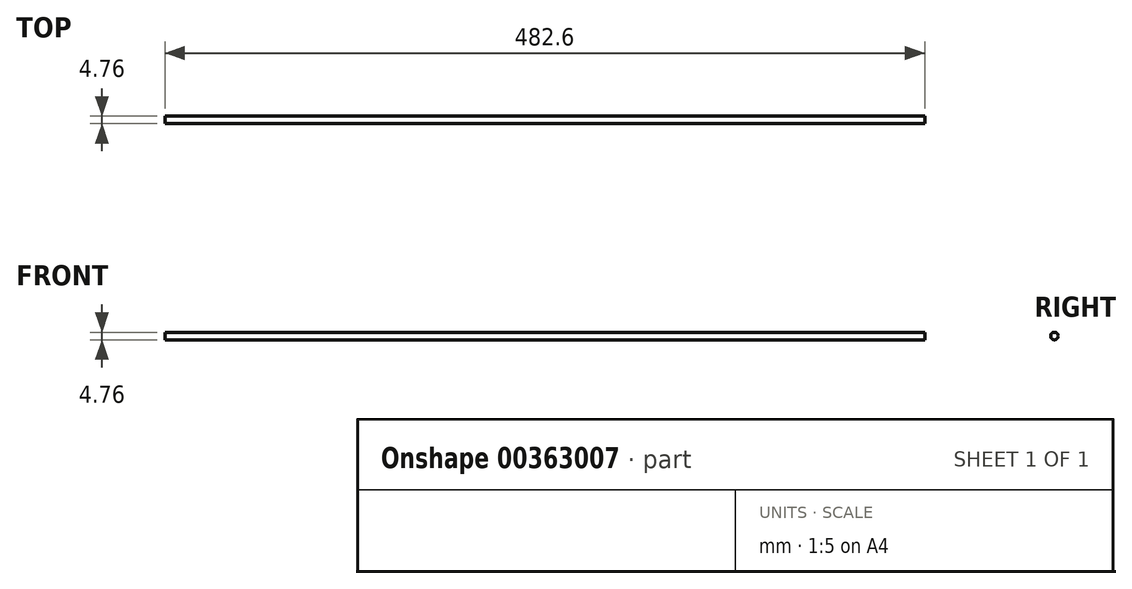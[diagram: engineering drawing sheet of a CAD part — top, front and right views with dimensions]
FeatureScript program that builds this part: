
annotation { "Feature Type Name" : "Feature", "Feature Type Description" : "" }
export const myFeature = defineFeature(function(context is Context, id is Id, definition is map)
    precondition{}
    {
        {
            var Q0;
            Q0=qCreatedBy(makeId("Right.planeOp"),FACE);
            var sketch = newSketch(context, id + "F0", { "sketchPlane" : qUnion([Q0])});
            skCircle(sketch, "E0", {"center": v(0, 0) * mm, "radius": 2.38 * mm});
            skSolve(sketch);
        }
        {
            var Q0;
            Q0=makeQuery(id+"F0.imprint","IMPRINT",FACE,{"disambiguationData":[TD([[makeQuery(id+"F0.imprint","IMPRINT",EDGE,{"derivedFrom":sQuery(id+"F0.wireOp",EDGE,"E0")}),1.0]])]});
            extrude(context, id + "F1", {"entities" : qUnion([Q0]), "depth" : 482.6 * mm});
        }
    });
